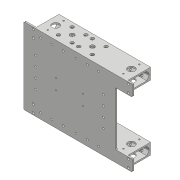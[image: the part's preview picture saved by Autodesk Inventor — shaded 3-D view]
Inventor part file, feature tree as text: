
AUTODESK INVENTOR PART (.ipt)
format: ipt  version: 2018 (Build 220112000, 112)  size: 3,772,416 bytes
history: native  units: mm
features: sketch x11, extrude x7, fillet x5, hole x4, mirror x4, projected_geometry x4, plane x2, imported_body x1, boolean_combine x1
ambient origin geometry x8: Origin, YZ Plane, XZ Plane, XY Plane, X Axis, Y Axis, Z Axis, Center Point
bodies: Solid1 (feature_tree), Solid2 (feature_tree)
feature tree (39):
  extrude  "Extrusion1"  Depth=172.0mm
  hole  "Hole1"  [1 undecoded]
  mirror  "Mirror1"
  extrude  "Extrusion2"  Depth=25.4mm TaperAngle=0.0deg
  extrude  "Extrusion3"  Depth=21.4376mm
  hole  "Hole2"  [1 undecoded]
  plane  "Work Plane2"
  mirror  "Mirror3"
  mirror  "Mirror4"
  hole  "Hole3"  [1 undecoded]
  extrude  "Extrusion4"  Depth=63.5mm TaperAngle=0.0deg
  fillet  "Fillet2"  Radius=25.4mm
  extrude  "Extrusion5"  Depth=38.1mm
  imported_body  "Base1"
  mirror  "Mirror5"
  boolean_combine  "Combine1"
  extrude  "Extrusion6"  Depth=2.0mm
  extrude  "Extrusion7"  Depth=56.5mm
  fillet  "Fillet3"  Radius=45.5mm
  fillet  "Fillet4"  Radius=1.6mm
  fillet  "Fillet5"  Radius=10.0mm
  hole  "Hole4"  [1 undecoded]
  fillet  "Fillet6"  Radius=90.0mm
  sketch  "Sketch1"  dims[d0=156.0mm d1=172.0mm]
  sketch  "Sketch2"  dims[d2=3.175mm d3=0.0mm d4=50.8mm]
  plane  "Work Plane1"
  sketch  "Sketch3"  dims[d5=12.7mm]
  projected_geometry  "Projected Loop1"
  sketch  "Sketch4"  dims[d7=4.5mm d8=6.0mm d9=9.4mm d10=2.0mm d11=90.0deg d12=8.0mm d13=20.594885mm d14=25.4mm d15=0.0mm]
  sketch  "Sketch5"  dims[d16=17.4625mm d17=21.4376mm]
  sketch  "Sketch6"  dims[d18=5.3mm d19=0.599mm d20=10.4mm d21=2.0mm d22=90.0deg d23=8.0mm d24=20.594885mm d26=66.0mm]
  projected_geometry  "Projected Loop2"
  sketch  "Sketch7"  dims[d28=4.5mm d29=6.0mm d30=9.4mm d31=2.0mm d32=90.0deg d33=8.0mm d34=20.594885mm d35=27.0mm]
  sketch  "Sketch8"  dims[d36=22.0mm d37=63.5mm d38=0.0mm d39=25.4mm]
  sketch  "Sketch9"  dims[d40=121.2mm d41=38.1mm]
  projected_geometry  "Projected Loop3"
  sketch  "Sketch10"  dims[d42=63.5mm d43=0.0mm d44=2.0mm]
  projected_geometry  "Projected Loop4"
  sketch  "Sketch11"  dims[d45=38.1mm d46=56.5mm d47=45.5mm d48=1.6mm d49=0.0mm d50=10.0mm d51=0.0mm d52=6.0mm d53=90.0mm d54=3.0mm d55=0.0mm d56=3.0mm d57=3.0mm d58=3.0mm d59=61.0mm d60=24.0mm d61=2.459mm d62=6.0mm d63=8.0mm d64=3.0mm d65=14.3117mm d66=8.8mm d67=20.594885mm d68=1.0mm]
note: 4 required parameter values undecoded (feature->parameter linkage not recoverable at this tier; creation-order binding heuristic only, values carry confidence <= 0.55)
